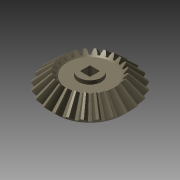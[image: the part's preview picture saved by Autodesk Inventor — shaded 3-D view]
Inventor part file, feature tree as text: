
AUTODESK INVENTOR PART (.ipt)
format: ipt  version: 2013 (Build 170138000, 138)  size: 808,960 bytes
history: native  units: mm
features: other x26, sketch x8, extrude x5, pattern_circular x3, loft x2, revolve x1, rib x1
ambient origin geometry x6: Origin, XZ Plane, X Axis, Y Axis, Z Axis, Center Point
bodies: Solid1 (feature_tree)
feature tree (46):
  other  "Top Point"
  other  "Mesh Plane2"
  other  "Teeth Body"
  other  "Start Point"
  other  "Tooth Plane"
  other  "Start Sketch"
  other  "End Point"
  other  "3D Sketch Right"
  other  "End Plane Right"
  loft  "Loft Right"
  pattern_circular  "Circular Pattern Right"  [2 undecoded]
  other  "3D Sketch Left"
  other  "End Plane Left"
  loft  "Loft Left"
  pattern_circular  "Circular Pattern Left"  [2 undecoded]
  other  "Fix Body"
  extrude  "Extrusion1"  Depth=9.888787mm
  extrude  "Extrusion2"  TaperAngle=0.0deg  [1 undecoded]
  sketch  "Sketch10"  dims[d4=11.951645mm]
  extrude  "Extrusion3"  Depth=240.0mm TaperAngle=0.0deg
  extrude  "Extrusion4"  TaperAngle=360.0deg  [1 undecoded]
  other  "iFeature2:1"
  revolve  "Revolution3"  [1 undecoded]
  rib  "Rib1"
  pattern_circular  "Circular Pattern4"  [2 undecoded]
  other  "Mesh Plane"
  other  "Top Plane"
  other  "Teeth Body Sketch"
  other  "End Plane"
  other  "End Sketch"
  other  "Helical Curve Left"
  other  "End Sketch Left"
  other  "Body Sketch"
  sketch  "Sketch6"  dims[d0=25.4mm d1=23.603949mm]
  other  "Srf1"
  other  "Helical Curve Right"
  other  "End Sketch Right"
  sketch  "Sketch8"  dims[d2=26.896709mm]
  sketch  "Sketch9"  dims[d3=6.35mm]
  sketch  "Sketch11"  dims[d5=90.0deg]
  sketch  "Sketch12"  dims[d7=6.504828mm]
  sketch  "Sketch13"  dims[d8=6.830589mm]
  sketch  "Sketch14"  dims[d9=15.427973mm d11=6.466417mm d12=4.169366mm d15=4.378167mm d16=9.888787mm d17=0.0mm d18=90.0deg d19=0.0mm d20=90.0deg d21=240.0mm d22=360.0deg d26=127.620481mm d27=4.572447mm d28=25.4mm d29=-7.853982mm d30=4.169366mm d31=4.378167mm d32=9.888787mm d35=0.0mm d37=0.0mm d39=0.0mm d40=90.0deg d41=240.0mm d42=360.0deg d46=90.0deg d47=90.0deg d51=1.308997mm d56=6.148598mm d57=19.717346mm d58=16.411112mm d59=12.638124mm d60=10.518945mm d61=12.638124mm d62=10.518945mm d63=90.0deg d64=90.0deg d65=127.620481mm d66=31.5mm d67=25.4mm d68=-7.853982mm d69=4.572447mm d70=4.378167mm d71=9.888787mm d72=4.169366mm d73=10.518945mm d74=12.638124mm d75=0.0mm d76=90.0deg d77=0.0mm d78=90.0deg d79=0.0mm d80=90.0deg d81=240.0mm d82=360.0deg d84=10.0mm d85=20.0mm d86=20.0mm d87=10.0mm d88=0.0mm d89=0.0mm d90=0.3556mm d91=-7.853982mm d92=1.1176mm d93=-7.853982mm d94=7.2644mm d95=9.525mm d96=0.0mm d97=1.1938mm d98=0.0mm d99=8.588765mm d100=4.0132mm d101=90.0deg d102=2.54mm d103=1.27mm d104=0.0mm d105=40.0mm d106=360.0deg d108=25.4mm d109=0.0mm d110=0.0mm d111=0.0mm]
  other  "Srf2"
  other  "Pitch Diameter"
  extrude  "ExtrusionSrf1"  Depth=4.169366mm
note: 9 required parameter values undecoded (feature->parameter linkage not recoverable at this tier; creation-order binding heuristic only, values carry confidence <= 0.55)